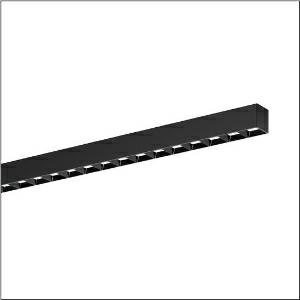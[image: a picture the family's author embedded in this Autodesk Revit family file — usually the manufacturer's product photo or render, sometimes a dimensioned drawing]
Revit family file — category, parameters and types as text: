
# Revit family: silica_r__21_51mx24dc4abb_c2b6
name_source: partatom
category: Lighting Fixtures
units: mm (PartAtom-declared; Revit-internal decimal feet)

## family parameters
Cut with Voids When Loaded = No
Host = Face
Light Source = No
Part Type = Normal
Room Calculation Point = No
Round Connector Dimension = Use Diameter
Shared = No

## types (1)
- --- (1 x LED, 10800 lm, 73.7 W, 4000K)
    Apparent Load = 74 VA
    CIE Flux Codes = 74 94 99 100 100
    Color Rendering = 80
    Color Temperature = 4000K
    Default Elevation = 1800 mm
    Description = Silica® 21, office luminaire, primary light control with darklight reflector, of PMMA, black, CAT 2 (L<= 3000cd/m²), light emission: direct distribution, primary light characteristic: asymmetric, installation type: surface-mounted, LED, rated luminous flux: 10.800lm, luminous efficacy: 147lm/W, light colour: 840, colour temperature: 4000K, control gear: DALI 2, with terminal, 3+2-pole, max. 2.5mm², mains connection: 220..240V, AC, 50/60Hz, rated input power: 73.7W, luminaire housing, of aluminium, matt jet black (RAL 9005), length: 3.004mm, width: 53mm, height: 53mm, protection rating (complete): IP20, insulation class (complete): insulation class I (protective earthing), certification: CE, permissible operating ambient temperature: 0..+35°C, standard: EN 50419, packaging unit: 1 piece
    Height = 53 mm
    Lamp = 1 x LED
    Lamp Light Flux = 10800 lm
    Lamp Power = 73.7 W
    Lamp count = 1
    Length = 3004 mm
    Luminous efficacy = 147 lm/W
    Manufacturer = Siteco
    ModVariant = No
    Model = 51MX24DC4ABB
    Mounting Place = Ceiling
    Mounting Type = Surface mounted
    Number of Poles = 1
    OnlyDefault = Yes
    Power Factor = 1
    Product Name = Silica® 21
    Product group = office luminaire | ceiling mounted
    ProductGroupID = 302
    Protection Class = Protection class I
    Protection Degree = IP 20
    RLX_Detail_Level = 1
    RLX_Emergency_Light_Flux = 0 lm
    RLX_Emergency_Type = 0
    RLX_Emergency_Type_DB = No
    RlxData = <blob elided: 64853 chars, md5=fc927ba7>
    Socket = socket
    Standby Power = 0 W
    System Light Flux = 10800 lm
    System Power = 74 W
    Type Comments = factory setting: luminous flux: 100 % | dim-lin: 254 | 418 mA
    Type Image = l_1335908.jpg
    URL = http://relux.com
    VarID = @adj_122866
    Voltage = 0 V
    Weight = 0.00 kg
    Width = 53 mm

## geometry (parser evidence)
native form markers: Blend x4, Sweep x8
no freeform markers — native parametric forms only
